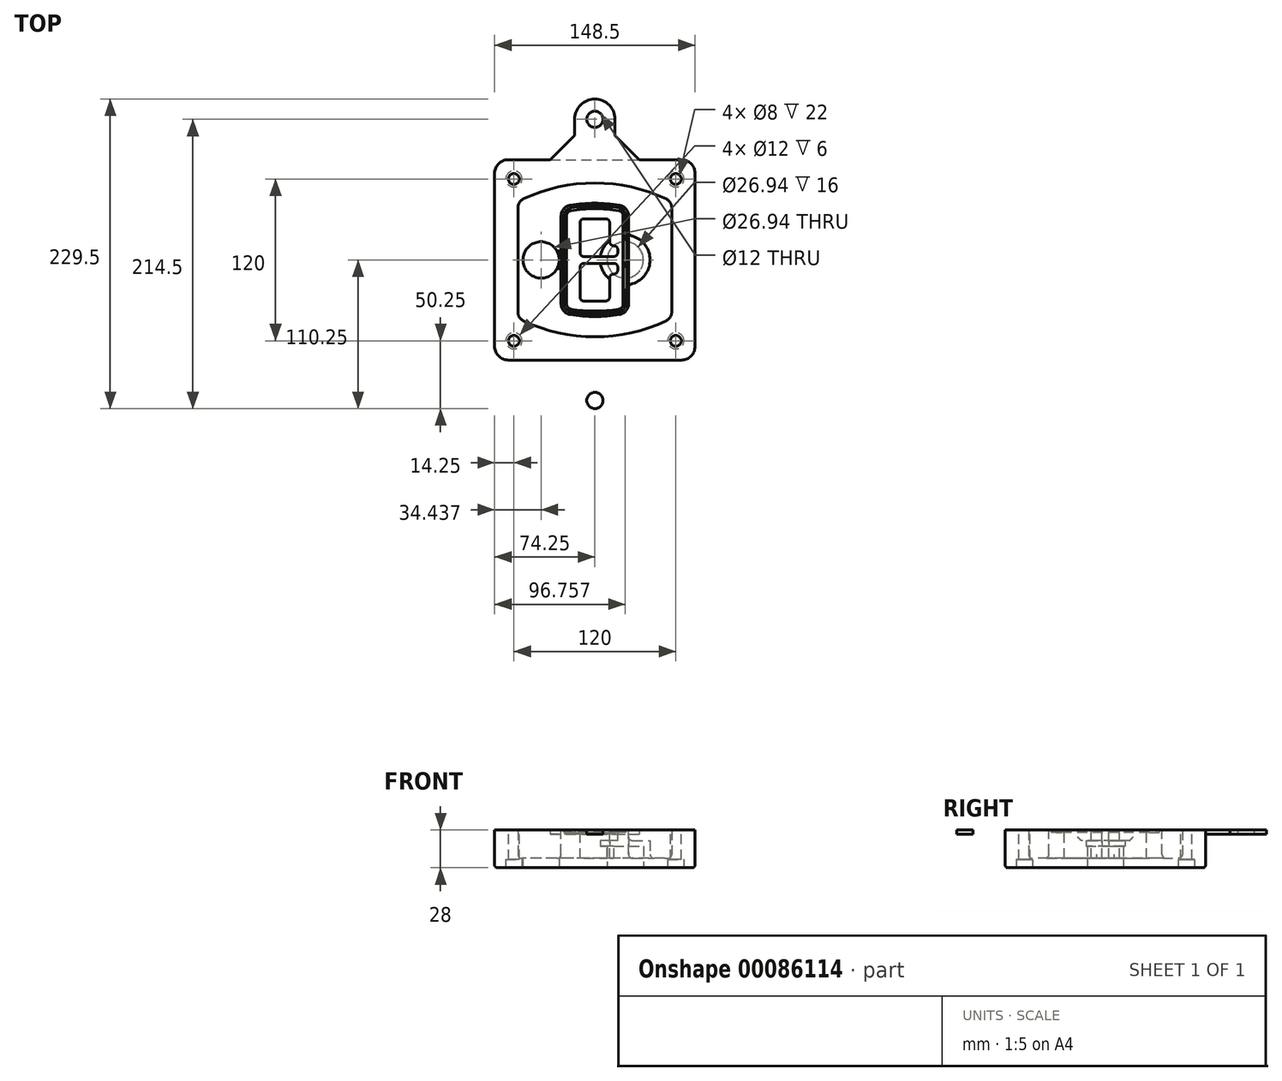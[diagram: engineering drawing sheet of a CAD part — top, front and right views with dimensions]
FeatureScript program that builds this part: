
annotation { "Feature Type Name" : "Feature", "Feature Type Description" : "" }
export const myFeature = defineFeature(function(context is Context, id is Id, definition is map)
    precondition{}
    {
        {
            var Q0;
            Q0=qCreatedBy(makeId("Top.planeOp"),FACE);
            var sketch = newSketch(context, id + "F0", { "sketchPlane" : qUnion([Q0])});
            skPoint(sketch, "E0.rect.middle", {"position": v(0, 0) * mm});
            skLineSegment(sketch, "E1.bottom", {"start": v(-64.25, -74.25) * mm, "end": v(64.25, -74.25) * mm});
            skLineSegment(sketch, "E1.top", {"start": v(-64.25, 74.25) * mm, "end": v(64.25, 74.25) * mm});
            skLineSegment(sketch, "E1.left", {"start": v(-74.25, -64.25) * mm, "end": v(-74.25, 64.25) * mm});
            skLineSegment(sketch, "E1.right", {"start": v(74.25, -64.25) * mm, "end": v(74.25, 64.25) * mm});
            skLineSegment(sketch, "E2", {"start": v(-74.25, 74.25) * mm, "end": v(74.25, -74.25) * mm, "construction": true});
            skLineSegment(sketch, "E3", {"start": v(74.25, 74.25) * mm, "end": v(-74.25, -74.25) * mm, "construction": true});
            skCircle(sketch, "E4", {"center": v(-60, 60) * mm, "radius": 4 * mm});
            skCircle(sketch, "E5", {"center": v(60, 60) * mm, "radius": 4 * mm});
            skCircle(sketch, "E6", {"center": v(60, -60) * mm, "radius": 4 * mm});
            skCircle(sketch, "E7", {"center": v(-60, -60) * mm, "radius": 4 * mm});
            skLineSegment(sketch, "E8", {"start": v(-60, 60) * mm, "end": v(60, 60) * mm, "construction": true});
            skLineSegment(sketch, "E9", {"start": v(60, 60) * mm, "end": v(60, -60) * mm, "construction": true});
            skLineSegment(sketch, "E10", {"start": v(60, -60) * mm, "end": v(-60, -60) * mm, "construction": true});
            skLineSegment(sketch, "E11", {"start": v(-60, -60) * mm, "end": v(-60, 60) * mm, "construction": true});
            skLineSegment(sketch, "E12", {"start": v(-60, 38.83) * mm, "end": v(-60, -38.83) * mm});
            skLineSegment(sketch, "E13", {"start": v(60, 38.83) * mm, "end": v(60, -38.83) * mm});
            skArc(sketch, "E14", {"start": v(54.26, 47.88) * mm, "mid": v(0, 60) * mm, "end": v(-54.26, 47.88) * mm});
            skArc(sketch, "E15", {"start": v(-54.26, -47.88) * mm, "mid": v(0, -60) * mm, "end": v(54.26, -47.88) * mm});
            skLineSegment(sketch, "E16", {"start": v(-60, 0) * mm, "end": v(60, 0) * mm, "construction": true});
            skPoint(sketch, "E17.visualSharp", {"position": v(-60, -45) * mm});
            skArc(sketch, "E17.filletArc", {"start": v(-60, -38.83) * mm, "mid": v(-58.44, -44.2) * mm, "end": v(-54.26, -47.88) * mm});
            skPoint(sketch, "E18.visualSharp", {"position": v(-60, 45) * mm});
            skArc(sketch, "E18.filletArc", {"start": v(-54.26, 47.88) * mm, "mid": v(-58.44, 44.2) * mm, "end": v(-60, 38.83) * mm});
            skPoint(sketch, "E19.visualSharp", {"position": v(60, 45) * mm});
            skArc(sketch, "E19.filletArc", {"start": v(60, 38.83) * mm, "mid": v(58.44, 44.2) * mm, "end": v(54.26, 47.88) * mm});
            skPoint(sketch, "E20.visualSharp", {"position": v(60, -45) * mm});
            skArc(sketch, "E20.filletArc", {"start": v(54.26, -47.88) * mm, "mid": v(58.44, -44.2) * mm, "end": v(60, -38.83) * mm});
            skPoint(sketch, "E21.visualSharp", {"position": v(-74.25, 74.25) * mm});
            skArc(sketch, "E21.filletArc", {"start": v(-64.25, 74.25) * mm, "mid": v(-71.32, 71.32) * mm, "end": v(-74.25, 64.25) * mm});
            skPoint(sketch, "E22.visualSharp", {"position": v(74.25, 74.25) * mm});
            skArc(sketch, "E22.filletArc", {"start": v(74.25, 64.25) * mm, "mid": v(71.32, 71.32) * mm, "end": v(64.25, 74.25) * mm});
            skPoint(sketch, "E23.visualSharp", {"position": v(74.25, -74.25) * mm});
            skArc(sketch, "E23.filletArc", {"start": v(64.25, -74.25) * mm, "mid": v(71.32, -71.32) * mm, "end": v(74.25, -64.25) * mm});
            skPoint(sketch, "E24.visualSharp", {"position": v(-74.25, -74.25) * mm});
            skArc(sketch, "E24.filletArc", {"start": v(-74.25, -64.25) * mm, "mid": v(-71.32, -71.32) * mm, "end": v(-64.25, -74.25) * mm});
            skArc(sketch, "E25.0", {"start": v(57, 38.83) * mm, "mid": v(55.9, 42.58) * mm, "end": v(52.98, 45.17) * mm});
            skLineSegment(sketch, "E25.1", {"start": v(57, 38.83) * mm, "end": v(57, -38.83) * mm});
            skArc(sketch, "E25.2", {"start": v(52.98, -45.17) * mm, "mid": v(55.9, -42.58) * mm, "end": v(57, -38.83) * mm});
            skArc(sketch, "E25.3", {"start": v(-52.98, -45.17) * mm, "mid": v(0, -57) * mm, "end": v(52.98, -45.17) * mm});
            skArc(sketch, "E25.4", {"start": v(-57, -38.83) * mm, "mid": v(-55.9, -42.58) * mm, "end": v(-52.98, -45.17) * mm});
            skArc(sketch, "E25.5", {"start": v(52.98, 45.17) * mm, "mid": v(0, 57) * mm, "end": v(-52.98, 45.17) * mm});
            skLineSegment(sketch, "E25.6", {"start": v(-57, 38.83) * mm, "end": v(-57, -38.83) * mm});
            skArc(sketch, "E25.7", {"start": v(-52.98, 45.17) * mm, "mid": v(-55.9, 42.58) * mm, "end": v(-57, 38.83) * mm});
            skArc(sketch, "E26.0", {"start": v(-55.96, 51.5) * mm, "mid": v(-61.82, 46.33) * mm, "end": v(-64, 38.83) * mm});
            skArc(sketch, "E26.1", {"start": v(55.96, 51.5) * mm, "mid": v(0, 64) * mm, "end": v(-55.96, 51.5) * mm});
            skArc(sketch, "E26.2", {"start": v(64, 38.83) * mm, "mid": v(61.82, 46.33) * mm, "end": v(55.96, 51.5) * mm});
            skLineSegment(sketch, "E26.3", {"start": v(64, 38.83) * mm, "end": v(64, -38.83) * mm});
            skArc(sketch, "E26.4", {"start": v(55.96, -51.5) * mm, "mid": v(61.82, -46.33) * mm, "end": v(64, -38.83) * mm});
            skLineSegment(sketch, "E26.5", {"start": v(-64, 38.83) * mm, "end": v(-64, -38.83) * mm});
            skArc(sketch, "E26.6", {"start": v(-55.96, -51.5) * mm, "mid": v(0, -64) * mm, "end": v(55.96, -51.5) * mm});
            skArc(sketch, "E26.7", {"start": v(-64, -38.83) * mm, "mid": v(-61.82, -46.33) * mm, "end": v(-55.96, -51.5) * mm});
            skSolve(sketch);
        }
        {
            var Q0;
            Q0=makeQuery(id+"F0.imprint","IMPRINT",FACE,{"disambiguationData":[TD([[makeQuery(id+"F0.imprint","IMPRINT",EDGE,{"derivedFrom":sQuery(id+"F0.wireOp",EDGE,"E1.bottom")}),1.0]])]});
            var Q1;
            Q1=makeQuery(id+"F0.imprint","IMPRINT",FACE,{"disambiguationData":[TD([[makeQuery(id+"F0.imprint","IMPRINT",EDGE,{"derivedFrom":sQuery(id+"F0.wireOp",EDGE,"E12")}),1.0]])]});
            var Q2;
            Q2=makeQuery(id+"F0.imprint","IMPRINT",FACE,{"disambiguationData":[TD([[makeQuery(id+"F0.imprint","IMPRINT",EDGE,{"derivedFrom":sQuery(id+"F0.wireOp",EDGE,"E25.0")}),1.0]])]});
            var Q3;
            Q3=makeQuery(id+"F0.imprint","IMPRINT",FACE,{"disambiguationData":[TD([[makeQuery(id+"F0.imprint","IMPRINT",EDGE,{"derivedFrom":sQuery(id+"F0.wireOp",EDGE,"E12")}),-1.0]])]});
            extrude(context, id + "F1", {"entities" : qUnion([Q0, Q1, Q2, Q3]), "oppositeDirection" : true, "depth" : 25 * mm});
        }
        {
            var Q0;
            Q0=makeQuery(id+"F0.imprint","IMPRINT",FACE,{"disambiguationData":[TD([[makeQuery(id+"F0.imprint","IMPRINT",EDGE,{"derivedFrom":sQuery(id+"F0.wireOp",EDGE,"E12")}),1.0]])]});
            extrude(context, id + "F2", {"entities" : qUnion([Q0]), "operationType" : NewBodyOperationType.ADD, "depth" : 3 * mm});
        }
        {
            var Q0;
            Q0=makeQuery(id+"F0.imprint","IMPRINT",FACE,{"disambiguationData":[TD([[makeQuery(id+"F0.imprint","IMPRINT",EDGE,{"derivedFrom":sQuery(id+"F0.wireOp",EDGE,"E25.0")}),1.0]])]});
            extrude(context, id + "F3", {"entities" : qUnion([Q0]), "operationType" : NewBodyOperationType.REMOVE, "oppositeDirection" : true, "depth" : 18 * mm});
        }
        {
            var Q0;
            Q0=makeQuery(id+"F2.opExtrude","CAP_FACE",FACE,{"disambiguationData":[OSD([sQuery(id+"F0.wireOp",EDGE,"E12"),sQuery(id+"F0.wireOp",EDGE,"E13"),sQuery(id+"F0.wireOp",EDGE,"E14"),sQuery(id+"F0.wireOp",EDGE,"E15"),sQuery(id+"F0.wireOp",EDGE,"E17.filletArc"),sQuery(id+"F0.wireOp",EDGE,"E18.filletArc"),sQuery(id+"F0.wireOp",EDGE,"E19.filletArc"),sQuery(id+"F0.wireOp",EDGE,"E20.filletArc"),sQuery(id+"F0.wireOp",EDGE,"E25.0"),sQuery(id+"F0.wireOp",EDGE,"E25.1"),sQuery(id+"F0.wireOp",EDGE,"E25.2"),sQuery(id+"F0.wireOp",EDGE,"E25.3"),sQuery(id+"F0.wireOp",EDGE,"E25.4"),sQuery(id+"F0.wireOp",EDGE,"E25.5"),sQuery(id+"F0.wireOp",EDGE,"E25.6"),sQuery(id+"F0.wireOp",EDGE,"E25.7")])],"isStart":false});
            var sketch = newSketch(context, id + "F4", { "sketchPlane" : qUnion([Q0])});
            skArc(sketch, "E27.0", {"start": v(-18.34, -40.45) * mm, "mid": v(0, -42) * mm, "end": v(18.34, -40.45) * mm});
            skArc(sketch, "E28.0", {"start": v(18.34, 40.45) * mm, "mid": v(0, 42) * mm, "end": v(-18.34, 40.45) * mm});
            skLineSegment(sketch, "E29", {"start": v(-25, 32.57) * mm, "end": v(-25, -32.57) * mm});
            skLineSegment(sketch, "E30", {"start": v(25, 32.57) * mm, "end": v(25, -32.57) * mm});
            skLineSegment(sketch, "E31", {"start": v(-25, 39.1) * mm, "end": v(25, 39.1) * mm, "construction": true});
            skLineSegment(sketch, "E32", {"start": v(-25, -39.1) * mm, "end": v(25, -39.1) * mm, "construction": true});
            skPoint(sketch, "E33.visualSharp", {"position": v(-25, 39.1) * mm});
            skArc(sketch, "E33.filletArc", {"start": v(-18.34, 40.45) * mm, "mid": v(-23.11, 37.73) * mm, "end": v(-25, 32.57) * mm});
            skPoint(sketch, "E34.visualSharp", {"position": v(25, 39.1) * mm});
            skArc(sketch, "E34.filletArc", {"start": v(25, 32.57) * mm, "mid": v(23.11, 37.73) * mm, "end": v(18.34, 40.45) * mm});
            skPoint(sketch, "E35.visualSharp", {"position": v(25, -39.1) * mm});
            skArc(sketch, "E35.filletArc", {"start": v(18.34, -40.45) * mm, "mid": v(23.11, -37.73) * mm, "end": v(25, -32.57) * mm});
            skPoint(sketch, "E36.visualSharp", {"position": v(-25, -39.1) * mm});
            skArc(sketch, "E36.filletArc", {"start": v(-25, -32.57) * mm, "mid": v(-23.11, -37.73) * mm, "end": v(-18.34, -40.45) * mm});
            skArc(sketch, "E37.0", {"start": v(52.98, 45.17) * mm, "mid": v(0, 57) * mm, "end": v(-52.98, 45.17) * mm});
            skArc(sketch, "E37.1", {"start": v(-52.98, 45.17) * mm, "mid": v(-55.9, 42.58) * mm, "end": v(-57, 38.83) * mm});
            skLineSegment(sketch, "E37.2", {"start": v(-57, 38.83) * mm, "end": v(-57, -38.83) * mm});
            skArc(sketch, "E37.3", {"start": v(-57, -38.83) * mm, "mid": v(-55.9, -42.58) * mm, "end": v(-52.98, -45.17) * mm});
            skArc(sketch, "E37.4", {"start": v(-52.98, -45.17) * mm, "mid": v(0, -57) * mm, "end": v(52.98, -45.17) * mm});
            skArc(sketch, "E37.5", {"start": v(52.98, -45.17) * mm, "mid": v(55.9, -42.58) * mm, "end": v(57, -38.83) * mm});
            skLineSegment(sketch, "E37.6", {"start": v(57, 38.83) * mm, "end": v(57, -38.83) * mm});
            skArc(sketch, "E37.7", {"start": v(57, 38.83) * mm, "mid": v(55.9, 42.58) * mm, "end": v(52.98, 45.17) * mm});
            skLineSegment(sketch, "E38.0", {"start": v(23, 32.57) * mm, "end": v(23, -32.57) * mm});
            skArc(sketch, "E38.1", {"start": v(18, -38.48) * mm, "mid": v(21.58, -36.44) * mm, "end": v(23, -32.57) * mm});
            skArc(sketch, "E38.2", {"start": v(-18, -38.48) * mm, "mid": v(0, -40) * mm, "end": v(18, -38.48) * mm});
            skArc(sketch, "E38.3", {"start": v(-23, -32.57) * mm, "mid": v(-21.58, -36.44) * mm, "end": v(-18, -38.48) * mm});
            skLineSegment(sketch, "E38.4", {"start": v(-23, 32.57) * mm, "end": v(-23, -32.57) * mm});
            skArc(sketch, "E38.5", {"start": v(23, 32.57) * mm, "mid": v(21.58, 36.44) * mm, "end": v(18, 38.48) * mm});
            skArc(sketch, "E38.6", {"start": v(-18, 38.48) * mm, "mid": v(-21.58, 36.44) * mm, "end": v(-23, 32.57) * mm});
            skArc(sketch, "E38.7", {"start": v(18, 38.48) * mm, "mid": v(0, 40) * mm, "end": v(-18, 38.48) * mm});
            skArc(sketch, "E39.0", {"start": v(21, 32.57) * mm, "mid": v(20.06, 35.15) * mm, "end": v(17.67, 36.5) * mm});
            skLineSegment(sketch, "E39.1", {"start": v(21, 32.57) * mm, "end": v(21, -32.57) * mm});
            skArc(sketch, "E39.2", {"start": v(17.67, -36.5) * mm, "mid": v(20.06, -35.15) * mm, "end": v(21, -32.57) * mm});
            skArc(sketch, "E39.3", {"start": v(-17.67, -36.5) * mm, "mid": v(0, -38) * mm, "end": v(17.67, -36.5) * mm});
            skArc(sketch, "E39.4", {"start": v(-21, -32.57) * mm, "mid": v(-20.06, -35.15) * mm, "end": v(-17.67, -36.5) * mm});
            skArc(sketch, "E39.5", {"start": v(17.67, 36.5) * mm, "mid": v(0, 38) * mm, "end": v(-17.67, 36.5) * mm});
            skLineSegment(sketch, "E39.6", {"start": v(-21, 32.57) * mm, "end": v(-21, -32.57) * mm});
            skArc(sketch, "E39.7", {"start": v(-17.67, 36.5) * mm, "mid": v(-20.06, 35.15) * mm, "end": v(-21, 32.57) * mm});
            skLineSegment(sketch, "E40", {"start": v(-25, 0) * mm, "end": v(25, 0) * mm, "construction": true});
            skLineSegment(sketch, "E41", {"start": v(-11, 5.5) * mm, "end": v(-11, 27.5) * mm});
            skLineSegment(sketch, "E42", {"start": v(-8, 30.5) * mm, "end": v(8, 30.5) * mm});
            skLineSegment(sketch, "E43", {"start": v(11, 27.5) * mm, "end": v(11, 13.5) * mm});
            skLineSegment(sketch, "E44", {"start": v(14, 10.5) * mm, "end": v(14, 10.5) * mm});
            skLineSegment(sketch, "E45", {"start": v(17, 7.5) * mm, "end": v(17, 5.5) * mm});
            skLineSegment(sketch, "E46", {"start": v(14, 2.5) * mm, "end": v(-8, 2.5) * mm});
            skPoint(sketch, "E47.visualSharp", {"position": v(-11, 30.5) * mm});
            skArc(sketch, "E47.filletArc", {"start": v(-8, 30.5) * mm, "mid": v(-10.12, 29.62) * mm, "end": v(-11, 27.5) * mm});
            skPoint(sketch, "E48.visualSharp", {"position": v(11, 30.5) * mm});
            skArc(sketch, "E48.filletArc", {"start": v(11, 27.5) * mm, "mid": v(10.12, 29.62) * mm, "end": v(8, 30.5) * mm});
            skPoint(sketch, "E49.visualSharp", {"position": v(11, 10.5) * mm});
            skArc(sketch, "E49.filletArc", {"start": v(11, 13.5) * mm, "mid": v(11.88, 11.38) * mm, "end": v(14, 10.5) * mm});
            skPoint(sketch, "E50.visualSharp", {"position": v(17, 10.5) * mm});
            skArc(sketch, "E50.filletArc", {"start": v(17, 7.5) * mm, "mid": v(16.12, 9.62) * mm, "end": v(14, 10.5) * mm});
            skPoint(sketch, "E51.visualSharp", {"position": v(17, 2.5) * mm});
            skArc(sketch, "E51.filletArc", {"start": v(14, 2.5) * mm, "mid": v(16.12, 3.38) * mm, "end": v(17, 5.5) * mm});
            skPoint(sketch, "E52.visualSharp", {"position": v(-11, 2.5) * mm});
            skArc(sketch, "E52.filletArc", {"start": v(-11, 5.5) * mm, "mid": v(-10.12, 3.38) * mm, "end": v(-8, 2.5) * mm});
            skLineSegment(sketch, "E53.0.MirrorCS", {"start": v(14, -2.5) * mm, "end": v(-8, -2.5) * mm});
            skArc(sketch, "E54.0.MirrorCS", {"start": v(-11, -5.5) * mm, "mid": v(-10.12, -3.38) * mm, "end": v(-8, -2.5) * mm});
            skLineSegment(sketch, "E55.0.MirrorCS", {"start": v(-11, -5.5) * mm, "end": v(-11, -27.5) * mm});
            skArc(sketch, "E56.0.MirrorCS", {"start": v(-8, -30.5) * mm, "mid": v(-10.12, -29.62) * mm, "end": v(-11, -27.5) * mm});
            skLineSegment(sketch, "E57.0.MirrorCS", {"start": v(-8, -30.5) * mm, "end": v(8, -30.5) * mm});
            skArc(sketch, "E58.0.MirrorCS", {"start": v(11, -27.5) * mm, "mid": v(10.12, -29.62) * mm, "end": v(8, -30.5) * mm});
            skLineSegment(sketch, "E59.0.MirrorCS", {"start": v(11, -27.5) * mm, "end": v(11, -13.5) * mm});
            skArc(sketch, "E60.0.MirrorCS", {"start": v(11, -13.5) * mm, "mid": v(11.88, -11.38) * mm, "end": v(14, -10.5) * mm});
            skArc(sketch, "E61.0.MirrorCS", {"start": v(17, -7.5) * mm, "mid": v(16.12, -9.62) * mm, "end": v(14, -10.5) * mm});
            skLineSegment(sketch, "E62.0.MirrorCS", {"start": v(17, -7.5) * mm, "end": v(17, -5.5) * mm});
            skArc(sketch, "E63.0.MirrorCS", {"start": v(14, -2.5) * mm, "mid": v(16.12, -3.38) * mm, "end": v(17, -5.5) * mm});
            skSolve(sketch);
        }
        {
            var Q0;
            Q0=makeQuery(id+"F4.imprint","IMPRINT",FACE,{"disambiguationData":[TD([[makeQuery(id+"F4.imprint","IMPRINT",EDGE,{"derivedFrom":sQuery(id+"F4.wireOp",EDGE,"E27.0")}),1.0]])]});
            var Q1;
            Q1=makeQuery(id+"F4.imprint","IMPRINT",FACE,{"disambiguationData":[TD([[makeQuery(id+"F4.imprint","IMPRINT",EDGE,{"derivedFrom":sQuery(id+"F4.wireOp",EDGE,"E38.0")}),-1.0]])]});
            var Q2;
            Q2=makeQuery(id+"F4.imprint","IMPRINT",FACE,{"disambiguationData":[TD([[makeQuery(id+"F4.imprint","IMPRINT",EDGE,{"derivedFrom":sQuery(id+"F4.wireOp",EDGE,"E39.0")}),1.0]])]});
            extrude(context, id + "F5", {"entities" : qUnion([Q0, Q1, Q2]), "operationType" : NewBodyOperationType.ADD, "endBound" : BoundingType.UP_TO_NEXT, "oppositeDirection" : true, "depth" : 25 * mm});
        }
        {
            var Q0;
            Q0=makeQuery(id+"F4.imprint","IMPRINT",FACE,{"disambiguationData":[TD([[makeQuery(id+"F4.imprint","IMPRINT",EDGE,{"derivedFrom":sQuery(id+"F4.wireOp",EDGE,"E38.0")}),-1.0]])]});
            extrude(context, id + "F6", {"entities" : qUnion([Q0]), "operationType" : NewBodyOperationType.REMOVE, "oppositeDirection" : true, "depth" : 2 * mm});
        }
        {
            var Q0;
            Q0=makeQuery(id+"F1.opExtrude","CAP_FACE",FACE,{"disambiguationData":[OSD([sQuery(id+"F0.wireOp",EDGE,"E1.bottom"),sQuery(id+"F0.wireOp",EDGE,"E1.top"),sQuery(id+"F0.wireOp",EDGE,"E1.left"),sQuery(id+"F0.wireOp",EDGE,"E1.right"),sQuery(id+"F0.wireOp",EDGE,"E4"),sQuery(id+"F0.wireOp",EDGE,"E5"),sQuery(id+"F0.wireOp",EDGE,"E6"),sQuery(id+"F0.wireOp",EDGE,"E7"),sQuery(id+"F0.wireOp",EDGE,"E21.filletArc"),sQuery(id+"F0.wireOp",EDGE,"E22.filletArc"),sQuery(id+"F0.wireOp",EDGE,"E23.filletArc"),sQuery(id+"F0.wireOp",EDGE,"E24.filletArc")])],"isStart":false});
            var sketch = newSketch(context, id + "F7", { "sketchPlane" : qUnion([Q0])});
            skCircle(sketch, "E64", {"center": v(22.5, 0) * mm, "radius": 13.47 * mm});
            skCircle(sketch, "E65", {"center": v(-39.81, 0) * mm, "radius": 13.47 * mm});
            skLineSegment(sketch, "E66", {"start": v(74.25, 0) * mm, "end": v(-74.25, 0) * mm});
            skCircle(sketch, "E67", {"center": v(22.5, 0) * mm, "radius": 18.47 * mm});
            skCircle(sketch, "E68", {"center": v(60, -60) * mm, "radius": 6 * mm});
            skCircle(sketch, "E69", {"center": v(-60, -60) * mm, "radius": 6 * mm});
            skCircle(sketch, "E70", {"center": v(-60, 60) * mm, "radius": 6 * mm});
            skCircle(sketch, "E71", {"center": v(60, 60) * mm, "radius": 6 * mm});
            skSolve(sketch);
        }
        {
            var Q0;
            {var subQ1=sQuery(id+"F7.wireOp",EDGE,"E66");var subQ4=sQuery(id+"F7.wireOp",EDGE,"E64");var subQ6=makeQuery(id+"F7.imprint","INTERSECT",VERTEX,{"disambiguationData":[OD(0.0)],"derivedFrom":[subQ4,subQ1]});Q0=makeQuery(id+"F7.imprint","IMPRINT",FACE,{"disambiguationData":[TD([[makeQuery(id+"F7.imprint","IMPRINT",EDGE,{"disambiguationData":[TD([[subQ6,-1.0]])],"derivedFrom":subQ4}),-1.0]])]});}
            var Q1;
            {var subQ0=sQuery(id+"F7.wireOp",EDGE,"E66");var subQ1=sQuery(id+"F7.wireOp",EDGE,"E64");var subQ3=makeQuery(id+"F7.imprint","INTERSECT",VERTEX,{"disambiguationData":[OD(0.0)],"derivedFrom":[subQ1,subQ0]});Q1=makeQuery(id+"F7.imprint","IMPRINT",FACE,{"disambiguationData":[TD([[makeQuery(id+"F7.imprint","IMPRINT",EDGE,{"disambiguationData":[TD([[subQ3,-1.0]])],"derivedFrom":subQ1}),1.0]])]});}
            var Q2;
            {var subQ0=sQuery(id+"F7.wireOp",EDGE,"E66");var subQ1=sQuery(id+"F7.wireOp",EDGE,"E64");var subQ3=makeQuery(id+"F7.imprint","INTERSECT",VERTEX,{"disambiguationData":[OD(0.0)],"derivedFrom":[subQ1,subQ0]});Q2=makeQuery(id+"F7.imprint","IMPRINT",FACE,{"disambiguationData":[TD([[makeQuery(id+"F7.imprint","IMPRINT",EDGE,{"disambiguationData":[TD([[subQ3,1.0]])],"derivedFrom":subQ1}),1.0]])]});}
            var Q3;
            {var subQ1=sQuery(id+"F7.wireOp",EDGE,"E66");var subQ4=sQuery(id+"F7.wireOp",EDGE,"E64");var subQ6=makeQuery(id+"F7.imprint","INTERSECT",VERTEX,{"disambiguationData":[OD(0.0)],"derivedFrom":[subQ4,subQ1]});Q3=makeQuery(id+"F7.imprint","IMPRINT",FACE,{"disambiguationData":[TD([[makeQuery(id+"F7.imprint","IMPRINT",EDGE,{"disambiguationData":[TD([[subQ6,1.0]])],"derivedFrom":subQ4}),-1.0]])]});}
            extrude(context, id + "F8", {"entities" : qUnion([Q0, Q1, Q2, Q3]), "operationType" : NewBodyOperationType.ADD, "oppositeDirection" : true, "depth" : 20 * mm});
        }
        {
            var Q0;
            {var subQ0=sQuery(id+"F7.wireOp",EDGE,"E66");var subQ1=sQuery(id+"F7.wireOp",EDGE,"E64");var subQ3=makeQuery(id+"F7.imprint","INTERSECT",VERTEX,{"disambiguationData":[OD(0.0)],"derivedFrom":[subQ1,subQ0]});Q0=makeQuery(id+"F7.imprint","IMPRINT",FACE,{"disambiguationData":[TD([[makeQuery(id+"F7.imprint","IMPRINT",EDGE,{"disambiguationData":[TD([[subQ3,-1.0]])],"derivedFrom":subQ1}),1.0]])]});}
            var Q1;
            {var subQ0=sQuery(id+"F7.wireOp",EDGE,"E66");var subQ1=sQuery(id+"F7.wireOp",EDGE,"E64");var subQ3=makeQuery(id+"F7.imprint","INTERSECT",VERTEX,{"disambiguationData":[OD(0.0)],"derivedFrom":[subQ1,subQ0]});Q1=makeQuery(id+"F7.imprint","IMPRINT",FACE,{"disambiguationData":[TD([[makeQuery(id+"F7.imprint","IMPRINT",EDGE,{"disambiguationData":[TD([[subQ3,1.0]])],"derivedFrom":subQ1}),1.0]])]});}
            extrude(context, id + "F9", {"entities" : qUnion([Q0, Q1]), "operationType" : NewBodyOperationType.REMOVE, "oppositeDirection" : true, "depth" : 16 * mm});
        }
        {
            var Q0;
            {var subQ0=sQuery(id+"F7.wireOp",EDGE,"E66");var subQ1=sQuery(id+"F7.wireOp",EDGE,"E65");var subQ3=makeQuery(id+"F7.imprint","INTERSECT",VERTEX,{"disambiguationData":[OD(0.0)],"derivedFrom":[subQ1,subQ0]});Q0=makeQuery(id+"F7.imprint","IMPRINT",FACE,{"disambiguationData":[TD([[makeQuery(id+"F7.imprint","IMPRINT",EDGE,{"disambiguationData":[TD([[subQ3,-1.0]])],"derivedFrom":subQ1}),1.0]])]});}
            var Q1;
            {var subQ0=sQuery(id+"F7.wireOp",EDGE,"E66");var subQ1=sQuery(id+"F7.wireOp",EDGE,"E65");var subQ3=makeQuery(id+"F7.imprint","INTERSECT",VERTEX,{"disambiguationData":[OD(0.0)],"derivedFrom":[subQ1,subQ0]});Q1=makeQuery(id+"F7.imprint","IMPRINT",FACE,{"disambiguationData":[TD([[makeQuery(id+"F7.imprint","IMPRINT",EDGE,{"disambiguationData":[TD([[subQ3,1.0]])],"derivedFrom":subQ1}),1.0]])]});}
            extrude(context, id + "F10", {"entities" : qUnion([Q0, Q1]), "operationType" : NewBodyOperationType.REMOVE, "oppositeDirection" : true, "depth" : 25 * mm});
        }
        {
            var Q0;
            Q0=makeQuery(id+"F7.imprint","IMPRINT",FACE,{"disambiguationData":[TD([[makeQuery(id+"F7.imprint","IMPRINT",EDGE,{"derivedFrom":sQuery(id+"F7.wireOp",EDGE,"E68")}),1.0]])]});
            var Q1;
            Q1=makeQuery(id+"F7.imprint","IMPRINT",FACE,{"disambiguationData":[TD([[makeQuery(id+"F7.imprint","IMPRINT",EDGE,{"derivedFrom":makeQuery(id+"F1.opExtrude","CAP_EDGE",EDGE,{"disambiguationData":[OSD([sQuery(id+"F0.wireOp",EDGE,"E5")])],"isStart":false})}),-1.0]])]});
            var Q2;
            Q2=makeQuery(id+"F7.imprint","IMPRINT",FACE,{"disambiguationData":[TD([[makeQuery(id+"F7.imprint","IMPRINT",EDGE,{"derivedFrom":sQuery(id+"F7.wireOp",EDGE,"E69")}),1.0]])]});
            var Q3;
            Q3=makeQuery(id+"F7.imprint","IMPRINT",FACE,{"disambiguationData":[TD([[makeQuery(id+"F7.imprint","IMPRINT",EDGE,{"derivedFrom":makeQuery(id+"F1.opExtrude","CAP_EDGE",EDGE,{"disambiguationData":[OSD([sQuery(id+"F0.wireOp",EDGE,"E4")])],"isStart":false})}),-1.0]])]});
            var Q4;
            Q4=makeQuery(id+"F7.imprint","IMPRINT",FACE,{"disambiguationData":[TD([[makeQuery(id+"F7.imprint","IMPRINT",EDGE,{"derivedFrom":sQuery(id+"F7.wireOp",EDGE,"E70")}),1.0]])]});
            var Q5;
            Q5=makeQuery(id+"F7.imprint","IMPRINT",FACE,{"disambiguationData":[TD([[makeQuery(id+"F7.imprint","IMPRINT",EDGE,{"derivedFrom":makeQuery(id+"F1.opExtrude","CAP_EDGE",EDGE,{"disambiguationData":[OSD([sQuery(id+"F0.wireOp",EDGE,"E7")])],"isStart":false})}),-1.0]])]});
            var Q6;
            Q6=makeQuery(id+"F7.imprint","IMPRINT",FACE,{"disambiguationData":[TD([[makeQuery(id+"F7.imprint","IMPRINT",EDGE,{"derivedFrom":sQuery(id+"F7.wireOp",EDGE,"E71")}),1.0]])]});
            var Q7;
            Q7=makeQuery(id+"F7.imprint","IMPRINT",FACE,{"disambiguationData":[TD([[makeQuery(id+"F7.imprint","IMPRINT",EDGE,{"derivedFrom":makeQuery(id+"F1.opExtrude","CAP_EDGE",EDGE,{"disambiguationData":[OSD([sQuery(id+"F0.wireOp",EDGE,"E6")])],"isStart":false})}),-1.0]])]});
            extrude(context, id + "F11", {"entities" : qUnion([Q0, Q1, Q2, Q3, Q4, Q5, Q6, Q7]), "operationType" : NewBodyOperationType.REMOVE, "oppositeDirection" : true, "depth" : 6 * mm});
        }
        {
            var Q0;
            Q0=makeQuery(id+"F9.boolean.opBoolean","COPY",FACE,{"derivedFrom":makeQuery(id+"F9.opExtrude","CAP_FACE",FACE,{"disambiguationData":[OSD([sQuery(id+"F7.wireOp",EDGE,"E64")])],"isStart":false})});
            var sketch = newSketch(context, id + "F12", { "sketchPlane" : qUnion([Q0])});
            skArc(sketch, "E72.0", {"start": v(11, 14.45) * mm, "mid": v(6.45, 9.13) * mm, "end": v(4.2, 2.5) * mm});
            skArc(sketch, "E72.1", {"start": v(4.2, -2.5) * mm, "mid": v(6.45, -9.13) * mm, "end": v(11, -14.45) * mm});
            skLineSegment(sketch, "E73", {"start": v(4.2, -2.5) * mm, "end": v(14, -2.5) * mm});
            skLineSegment(sketch, "E74.0", {"start": v(14, 2.5) * mm, "end": v(4.2, 2.5) * mm});
            skArc(sketch, "E74.1", {"start": v(14, 2.5) * mm, "mid": v(16.12, 3.38) * mm, "end": v(17, 5.5) * mm});
            skLineSegment(sketch, "E74.2", {"start": v(17, 7.5) * mm, "end": v(17, 5.5) * mm});
            skArc(sketch, "E74.3", {"start": v(17, 7.5) * mm, "mid": v(16.12, 9.62) * mm, "end": v(14, 10.5) * mm});
            skArc(sketch, "E74.4", {"start": v(11, 13.5) * mm, "mid": v(11.88, 11.38) * mm, "end": v(14, 10.5) * mm});
            skLineSegment(sketch, "E74.5", {"start": v(11, 14.45) * mm, "end": v(11, 13.5) * mm});
            skLineSegment(sketch, "E74.7", {"start": v(14, -2.5) * mm, "end": v(4.2, -2.5) * mm});
            skArc(sketch, "E74.8", {"start": v(14, -2.5) * mm, "mid": v(16.12, -3.38) * mm, "end": v(17, -5.5) * mm});
            skLineSegment(sketch, "E74.9", {"start": v(17, -7.5) * mm, "end": v(17, -5.5) * mm});
            skArc(sketch, "E74.10", {"start": v(17, -7.5) * mm, "mid": v(16.12, -9.62) * mm, "end": v(14, -10.5) * mm});
            skArc(sketch, "E74.11", {"start": v(11, -13.5) * mm, "mid": v(11.88, -11.38) * mm, "end": v(14, -10.5) * mm});
            skLineSegment(sketch, "E74.12", {"start": v(11, -14.45) * mm, "end": v(11, -13.5) * mm});
            skPoint(sketch, "E75.orphan", {"position": v(11, -27.5) * mm});
            skPoint(sketch, "E76.orphan", {"position": v(-8, -2.5) * mm});
            skPoint(sketch, "E77.orphan", {"position": v(-8, 2.5) * mm});
            skPoint(sketch, "E78.orphan", {"position": v(11, 27.5) * mm});
            skSolve(sketch);
        }
        {
            var Q0;
            {var subQ7=sQuery(id+"F12.wireOp",EDGE,"E72.0");var subQ14=sQuery(id+"F12.wireOp",EDGE,"E72.1");var subQ16=sQuery(id+"F12.wireOp",EDGE,"E74.1");var subQ18=sQuery(id+"F12.wireOp",EDGE,"E74.8");Q0=qUnion([makeQuery(id+"F12.imprint","IMPRINT",FACE,{"disambiguationData":[TD([[makeQuery(id+"F12.imprint","IMPRINT",EDGE,{"derivedFrom":subQ7}),1.0]])]}),makeQuery(id+"F12.imprint","IMPRINT",FACE,{"disambiguationData":[TD([[makeQuery(id+"F12.imprint","IMPRINT",EDGE,{"derivedFrom":subQ14}),1.0]])]}),makeQuery(id+"F12.imprint","IMPRINT",FACE,{"disambiguationData":[TD([[makeQuery(id+"F12.imprint","IMPRINT",EDGE,{"derivedFrom":subQ16}),1.0]])]}),makeQuery(id+"F12.imprint","IMPRINT",FACE,{"disambiguationData":[TD([[makeQuery(id+"F12.imprint","IMPRINT",EDGE,{"derivedFrom":subQ18}),-1.0]])]})]);}
            var Q1;
            Q1=makeQuery(id+"F5.boolean.opBoolean","SPLIT",FACE,{"disambiguationData":[TD([makeQuery(id+"F5.opExtrude","SWEPT_FACE",FACE,{"disambiguationData":[OSD([sQuery(id+"F4.wireOp",EDGE,"E41")])]})])],"derivedFrom":makeQuery(id+"F3.boolean.opBoolean","COPY",FACE,{"derivedFrom":makeQuery(id+"F3.opExtrude","CAP_FACE",FACE,{"disambiguationData":[OSD([sQuery(id+"F0.wireOp",EDGE,"E25.0"),sQuery(id+"F0.wireOp",EDGE,"E25.1"),sQuery(id+"F0.wireOp",EDGE,"E25.2"),sQuery(id+"F0.wireOp",EDGE,"E25.3"),sQuery(id+"F0.wireOp",EDGE,"E25.4"),sQuery(id+"F0.wireOp",EDGE,"E25.5"),sQuery(id+"F0.wireOp",EDGE,"E25.6"),sQuery(id+"F0.wireOp",EDGE,"E25.7")])],"isStart":false})})});
            extrude(context, id + "F13", {"entities" : qUnion([Q0]), "operationType" : NewBodyOperationType.REMOVE, "endBound" : BoundingType.UP_TO_SURFACE, "endBoundEntityFace" : qUnion([Q1]), "depth" : 25 * mm});
        }
        {
            var Q0;
            Q0=makeQuery(id+"F3.boolean.opBoolean","COPY",EDGE,{"derivedFrom":makeQuery(id+"F3.opExtrude","CAP_EDGE",EDGE,{"disambiguationData":[OSD([sQuery(id+"F0.wireOp",EDGE,"E25.6")])],"isStart":false})});
            var Q1;
            Q1=makeQuery(id+"F8.boolean.opBoolean","INTERSECT",EDGE,{"derivedFrom":[makeQuery(id+"F5.opExtrude","SWEPT_FACE",FACE,{"disambiguationData":[OSD([sQuery(id+"F4.wireOp",EDGE,"E30")])]}),makeQuery(id+"F8.opExtrude","CAP_FACE",FACE,{"disambiguationData":[OSD([sQuery(id+"F7.wireOp",EDGE,"E67")])],"isStart":false})]});
            var Q2;
            Q2=makeQuery(id+"F8.boolean.opBoolean","INTERSECT",EDGE,{"disambiguationData":[OD(1.0)],"derivedFrom":[makeQuery(id+"F5.opExtrude","SWEPT_FACE",FACE,{"disambiguationData":[OSD([sQuery(id+"F4.wireOp",EDGE,"E30")])]}),makeQuery(id+"F8.opExtrude","SWEPT_FACE",FACE,{"disambiguationData":[OSD([sQuery(id+"F7.wireOp",EDGE,"E67")])]})]});
            var Q3;
            {var subQ0=sQuery(id+"F4.wireOp",EDGE,"E30");Q3=makeQuery(id+"F8.boolean.opBoolean","SPLIT",EDGE,{"disambiguationData":[TD([makeQuery(id+"F5.opExtrude","SWEPT_FACE",FACE,{"disambiguationData":[OSD([sQuery(id+"F4.wireOp",EDGE,"E35.filletArc")])]})])],"derivedFrom":makeQuery(id+"F5.opExtrude","CAP_EDGE",EDGE,{"disambiguationData":[OSD([subQ0])],"isStart":false})});}
            var Q4;
            {var subQ0=sQuery(id+"F0.wireOp",EDGE,"E25.7");var subQ1=sQuery(id+"F0.wireOp",EDGE,"E25.1");var subQ2=sQuery(id+"F0.wireOp",EDGE,"E25.6");var subQ3=sQuery(id+"F0.wireOp",EDGE,"E25.5");var subQ4=sQuery(id+"F0.wireOp",EDGE,"E25.4");var subQ5=sQuery(id+"F0.wireOp",EDGE,"E25.0");var subQ6=sQuery(id+"F0.wireOp",EDGE,"E25.2");var subQ7=sQuery(id+"F0.wireOp",EDGE,"E25.3");Q4=makeQuery(id+"F8.boolean.opBoolean","INTERSECT",EDGE,{"derivedFrom":[makeQuery(id+"F5.boolean.opBoolean","SPLIT",FACE,{"disambiguationData":[TD([makeQuery(id+"F2.opExtrude","SWEPT_FACE",FACE,{"disambiguationData":[OSD([subQ5])]})])],"derivedFrom":makeQuery(id+"F3.boolean.opBoolean","COPY",FACE,{"derivedFrom":makeQuery(id+"F3.opExtrude","CAP_FACE",FACE,{"disambiguationData":[OSD([subQ5,subQ1,subQ6,subQ7,subQ4,subQ3,subQ2,subQ0])],"isStart":false})})}),makeQuery(id+"F8.opExtrude","SWEPT_FACE",FACE,{"disambiguationData":[OSD([sQuery(id+"F7.wireOp",EDGE,"E67")])]})]});}
            var Q5;
            Q5=makeQuery(id+"F8.boolean.opBoolean","INTERSECT",EDGE,{"disambiguationData":[OD(0.0)],"derivedFrom":[makeQuery(id+"F5.opExtrude","SWEPT_FACE",FACE,{"disambiguationData":[OSD([sQuery(id+"F4.wireOp",EDGE,"E30")])]}),makeQuery(id+"F8.opExtrude","SWEPT_FACE",FACE,{"disambiguationData":[OSD([sQuery(id+"F7.wireOp",EDGE,"E67")])]})]});
            fillet(context, id + "F14", {"entities" : qUnion([Q0, Q1, Q2, Q3, Q4, Q5]), "radius" : 3 * mm, "tangentPropagation" : true, "allowEdgeOverflow" : false});
        }
        {
            var Q0;
            Q0=makeQuery(id+"F1.opExtrude","CAP_EDGE",EDGE,{"disambiguationData":[OSD([sQuery(id+"F0.wireOp",EDGE,"E1.bottom")])],"isStart":false});
            fillet(context, id + "F15", {"entities" : qUnion([Q0]), "radius" : 2 * mm, "tangentPropagation" : true, "allowEdgeOverflow" : false});
        }
        {
            var Q0;
            {var subQ0=sQuery(id+"F0.wireOp",EDGE,"E22.filletArc");var subQ1=sQuery(id+"F0.wireOp",EDGE,"E7");var subQ2=sQuery(id+"F0.wireOp",EDGE,"E6");var subQ3=sQuery(id+"F0.wireOp",EDGE,"E5");var subQ4=sQuery(id+"F0.wireOp",EDGE,"E4");var subQ5=sQuery(id+"F0.wireOp",EDGE,"E1.bottom");var subQ6=sQuery(id+"F0.wireOp",EDGE,"E21.filletArc");var subQ7=sQuery(id+"F0.wireOp",EDGE,"E1.top");var subQ8=sQuery(id+"F0.wireOp",EDGE,"E1.left");var subQ9=sQuery(id+"F0.wireOp",EDGE,"E1.right");var subQ10=sQuery(id+"F0.wireOp",EDGE,"E23.filletArc");var subQ11=sQuery(id+"F0.wireOp",EDGE,"E24.filletArc");Q0=makeQuery(id+"F2.boolean.opBoolean","SPLIT",FACE,{"disambiguationData":[TD([makeQuery(id+"F1.opExtrude","SWEPT_FACE",FACE,{"disambiguationData":[OSD([subQ5])]})])],"derivedFrom":makeQuery(id+"F1.opExtrude","CAP_FACE",FACE,{"disambiguationData":[OSD([subQ5,subQ7,subQ8,subQ9,subQ4,subQ3,subQ2,subQ1,subQ6,subQ0,subQ10,subQ11])],"isStart":true})});}
            var sketch = newSketch(context, id + "F16", { "sketchPlane" : qUnion([Q0])});
            skLineSegment(sketch, "E79", {"start": v(0, 74.25) * mm, "end": v(0, 104.25) * mm, "construction": true});
            skCircle(sketch, "E80", {"center": v(0, 104.25) * mm, "radius": 6 * mm});
            skArc(sketch, "E81", {"start": v(0, 119.25) * mm, "mid": v(-10.6, 114.86) * mm, "end": v(-15, 104.25) * mm});
            skArc(sketch, "E82", {"start": v(0, 119.25) * mm, "mid": v(10.6, 114.86) * mm, "end": v(15, 104.25) * mm});
            skLineSegment(sketch, "E83", {"start": v(-15, 104.25) * mm, "end": v(-15, 92.25) * mm});
            skLineSegment(sketch, "E84", {"start": v(15, 104.25) * mm, "end": v(15, 92.25) * mm});
            skLineSegment(sketch, "E85", {"start": v(-15, 92.25) * mm, "end": v(-33, 74.25) * mm});
            skLineSegment(sketch, "E86", {"start": v(15, 92.25) * mm, "end": v(33, 74.25) * mm});
            skLineSegment(sketch, "E87", {"start": v(0, 0) * mm, "end": v(126.41, 0) * mm});
            skPoint(sketch, "E87.endSnap0", {"position": v(74.25, 0) * mm});
            skCircle(sketch, "E88.MirrorC", {"center": v(0, -104.25) * mm, "radius": 6 * mm});
            skLineSegment(sketch, "E89.MirrorCS", {"start": v(15, -104.25) * mm, "end": v(15, -92.25) * mm});
            skArc(sketch, "E90.MirrorCS", {"start": v(0, -119.25) * mm, "mid": v(10.6, -114.86) * mm, "end": v(15, -104.25) * mm});
            skArc(sketch, "E91.MirrorCS", {"start": v(0, -119.25) * mm, "mid": v(-10.6, -114.86) * mm, "end": v(-15, -104.25) * mm});
            skLineSegment(sketch, "E92.MirrorCS", {"start": v(-15, -104.25) * mm, "end": v(-15, -92.25) * mm});
            skLineSegment(sketch, "E93.MirrorCS", {"start": v(15, -92.25) * mm, "end": v(33, -74.25) * mm});
            skLineSegment(sketch, "E94.MirrorCS", {"start": v(-15, -92.25) * mm, "end": v(-33, -74.25) * mm});
            skSolve(sketch);
        }
        {
            var Q0;
            Q0=makeQuery(id+"F16.imprint","IMPRINT",FACE,{"disambiguationData":[TD([[makeQuery(id+"F16.imprint","IMPRINT",EDGE,{"derivedFrom":sQuery(id+"F16.wireOp",EDGE,"E80")}),-1.0]])]});
            var Q1;
            Q1=makeQuery(id+"F16.imprint","IMPRINT",FACE,{"disambiguationData":[TD([[makeQuery(id+"F16.imprint","IMPRINT",EDGE,{"derivedFrom":makeQuery(id+"F1.opExtrude","CAP_EDGE",EDGE,{"disambiguationData":[OSD([sQuery(id+"F0.wireOp",EDGE,"E1.left")])],"isStart":true})}),-1.0]])]});
            var Q2;
            Q2=makeQuery(id+"F16.imprint","IMPRINT",FACE,{"disambiguationData":[TD([[makeQuery(id+"F16.imprint","IMPRINT",EDGE,{"derivedFrom":sQuery(id+"F16.wireOp",EDGE,"E88.MirrorC")}),1.0]])]});
            var Q3;
            Q3=makeQuery(id+"F2.opExtrude","CAP_FACE",FACE,{"disambiguationData":[OSD([sQuery(id+"F0.wireOp",EDGE,"E12"),sQuery(id+"F0.wireOp",EDGE,"E13"),sQuery(id+"F0.wireOp",EDGE,"E14"),sQuery(id+"F0.wireOp",EDGE,"E15"),sQuery(id+"F0.wireOp",EDGE,"E17.filletArc"),sQuery(id+"F0.wireOp",EDGE,"E18.filletArc"),sQuery(id+"F0.wireOp",EDGE,"E19.filletArc"),sQuery(id+"F0.wireOp",EDGE,"E20.filletArc"),sQuery(id+"F0.wireOp",EDGE,"E25.0"),sQuery(id+"F0.wireOp",EDGE,"E25.1"),sQuery(id+"F0.wireOp",EDGE,"E25.2"),sQuery(id+"F0.wireOp",EDGE,"E25.3"),sQuery(id+"F0.wireOp",EDGE,"E25.4"),sQuery(id+"F0.wireOp",EDGE,"E25.5"),sQuery(id+"F0.wireOp",EDGE,"E25.6"),sQuery(id+"F0.wireOp",EDGE,"E25.7")])],"isStart":false});
            extrude(context, id + "F17", {"entities" : qUnion([Q0, Q1, Q2]), "operationType" : NewBodyOperationType.ADD, "endBound" : BoundingType.UP_TO_SURFACE, "endBoundEntityFace" : qUnion([Q3]), "depth" : 25 * mm});
        }
    });
